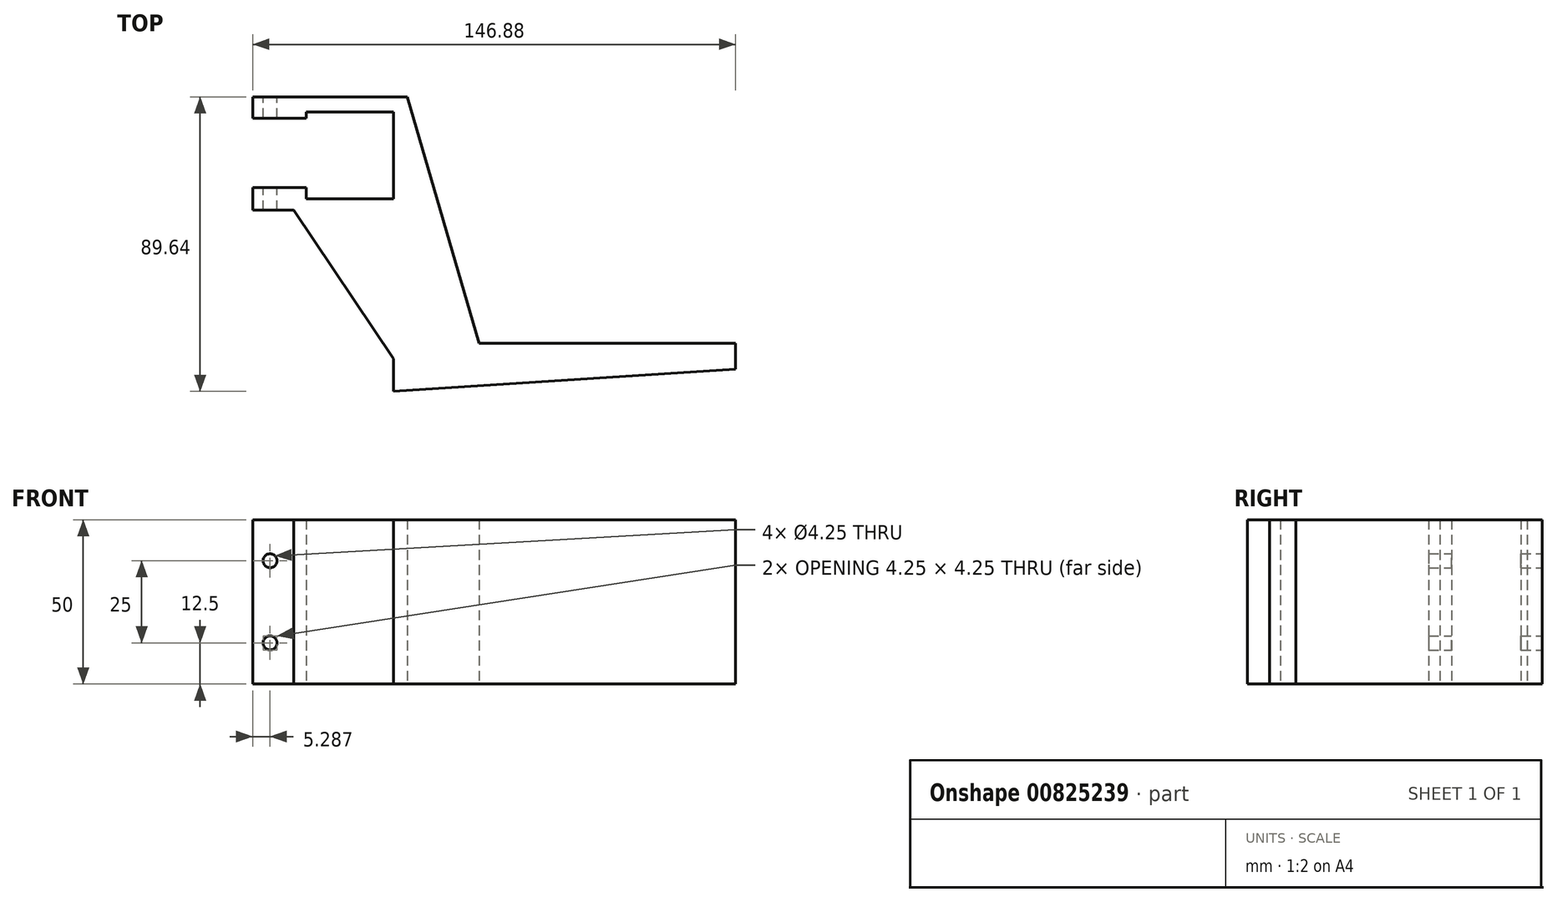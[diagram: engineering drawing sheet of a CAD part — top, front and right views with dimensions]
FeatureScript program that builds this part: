
annotation { "Feature Type Name" : "Feature", "Feature Type Description" : "" }
export const myFeature = defineFeature(function(context is Context, id is Id, definition is map)
    precondition{}
    {
        {
            var Q0;
            Q0=qCreatedBy(makeId("Top.planeOp"),FACE);
            var sketch = newSketch(context, id + "F0", { "sketchPlane" : qUnion([Q0])});
            skLineSegment(sketch, "E0", {"start": v(-30.27, 0) * mm, "end": v(-30.27, -1.89) * mm});
            skLineSegment(sketch, "E1", {"start": v(-30.27, -1.89) * mm, "end": v(-26.5, -1.89) * mm});
            skLineSegment(sketch, "E2", {"start": v(-26.5, -1.89) * mm, "end": v(-26.5, 0) * mm});
            skLineSegment(sketch, "E3", {"start": v(-26.5, 0) * mm, "end": v(0, 0) * mm});
            skLineSegment(sketch, "E4", {"start": v(0, 0) * mm, "end": v(0, -26.5) * mm});
            skLineSegment(sketch, "E5", {"start": v(0, -26.5) * mm, "end": v(-26.5, -26.5) * mm});
            skLineSegment(sketch, "E6", {"start": v(-30.27, -26.5) * mm, "end": v(-30.27, -29.91) * mm});
            skLineSegment(sketch, "E7", {"start": v(-30.27, -29.91) * mm, "end": v(0, -29.91) * mm});
            skLineSegment(sketch, "E8", {"start": v(0, -29.91) * mm, "end": v(4.22, -29.91) * mm});
            skLineSegment(sketch, "E9", {"start": v(4.22, -29.91) * mm, "end": v(4.22, 0) * mm});
            skLineSegment(sketch, "E10", {"start": v(4.22, 0) * mm, "end": v(4.22, 4.58) * mm});
            skLineSegment(sketch, "E11", {"start": v(4.22, 4.58) * mm, "end": v(-30.27, 4.58) * mm});
            skLineSegment(sketch, "E12", {"start": v(-30.27, 4.58) * mm, "end": v(-30.27, 0) * mm});
            skLineSegment(sketch, "E13", {"start": v(-26.5, -26.5) * mm, "end": v(-26.5, -22.97) * mm});
            skLineSegment(sketch, "E14", {"start": v(-26.5, -22.97) * mm, "end": v(-30.27, -22.97) * mm});
            skLineSegment(sketch, "E15", {"start": v(-30.27, -22.97) * mm, "end": v(-30.27, -26.5) * mm});
            skLineSegment(sketch, "E16", {"start": v(-30.27, 4.58) * mm, "end": v(-42.8, 4.58) * mm});
            skLineSegment(sketch, "E17", {"start": v(-42.8, 4.58) * mm, "end": v(-42.8, -1.89) * mm});
            skLineSegment(sketch, "E18", {"start": v(-42.8, -1.89) * mm, "end": v(-30.27, -1.89) * mm});
            skLineSegment(sketch, "E19", {"start": v(-30.27, -22.97) * mm, "end": v(-42.8, -22.97) * mm});
            skLineSegment(sketch, "E20", {"start": v(-42.8, -22.97) * mm, "end": v(-42.8, -29.91) * mm});
            skLineSegment(sketch, "E21", {"start": v(-42.8, -29.91) * mm, "end": v(-30.27, -29.91) * mm});
            skLineSegment(sketch, "E22", {"start": v(4.22, 4.58) * mm, "end": v(4.22, -70.37) * mm});
            skLineSegment(sketch, "E23", {"start": v(0, -29.91) * mm, "end": v(0, -75.04) * mm});
            skLineSegment(sketch, "E24", {"start": v(4.22, -70.37) * mm, "end": v(26.08, -70.37) * mm});
            skLineSegment(sketch, "E25", {"start": v(26.08, -70.37) * mm, "end": v(4.22, 4.58) * mm});
            skLineSegment(sketch, "E26", {"start": v(0, -75.04) * mm, "end": v(-30.27, -29.91) * mm});
            skLineSegment(sketch, "E27", {"start": v(0, -75.04) * mm, "end": v(0, -85.06) * mm});
            skLineSegment(sketch, "E28", {"start": v(104.1, -70.37) * mm, "end": v(104.1, -75.04) * mm});
            skLineSegment(sketch, "E29", {"start": v(104.1, -75.04) * mm, "end": v(104.1, -78.33) * mm});
            skLineSegment(sketch, "E30", {"start": v(26.08, -70.37) * mm, "end": v(104.1, -70.37) * mm});
            skLineSegment(sketch, "E31", {"start": v(0, -85.06) * mm, "end": v(104.1, -78.33) * mm});
            skSolve(sketch);
        }
        {
            var Q0;
            Q0=makeQuery(id+"F0.imprint","IMPRINT",FACE,{"disambiguationData":[TD([[makeQuery(id+"F0.imprint","IMPRINT",EDGE,{"derivedFrom":sQuery(id+"F0.wireOp",EDGE,"E0")}),1.0]])]});
            var Q1;
            Q1=makeQuery(id+"F0.imprint","IMPRINT",FACE,{"disambiguationData":[TD([[makeQuery(id+"F0.imprint","IMPRINT",EDGE,{"derivedFrom":sQuery(id+"F0.wireOp",EDGE,"E0")}),-1.0]])]});
            var Q2;
            Q2=makeQuery(id+"F0.imprint","IMPRINT",FACE,{"disambiguationData":[TD([[makeQuery(id+"F0.imprint","IMPRINT",EDGE,{"derivedFrom":sQuery(id+"F0.wireOp",EDGE,"E6")}),-1.0]])]});
            var Q3;
            Q3=makeQuery(id+"F0.imprint","IMPRINT",FACE,{"disambiguationData":[TD([[makeQuery(id+"F0.imprint","IMPRINT",EDGE,{"derivedFrom":sQuery(id+"F0.wireOp",EDGE,"E7")}),-1.0]])]});
            var Q4;
            Q4=makeQuery(id+"F0.imprint","IMPRINT",FACE,{"disambiguationData":[TD([[makeQuery(id+"F0.imprint","IMPRINT",EDGE,{"derivedFrom":sQuery(id+"F0.wireOp",EDGE,"i6da61lU-EC8u-8acG-F84r-jOoYWlgI5SIy")}),-1.0]])]});
            var Q5;
            {var subQ1=sQuery(id+"F0.wireOp",EDGE,"E8");Q5=makeQuery(id+"F0.imprint","IMPRINT",FACE,{"disambiguationData":[TD([[makeQuery(id+"F0.imprint","IMPRINT",EDGE,{"derivedFrom":subQ1}),-1.0]])]});}
            var Q6;
            {var subQ3=sQuery(id+"F0.wireOp",EDGE,"E24");Q6=makeQuery(id+"F0.imprint","IMPRINT",FACE,{"disambiguationData":[TD([[makeQuery(id+"F0.imprint","IMPRINT",EDGE,{"derivedFrom":subQ3}),1.0]])]});}
            extrude(context, id + "F1", {"entities" : qUnion([Q0, Q1, Q2, Q3, Q4, Q5, Q6]), "depth" : 50 * mm, "offsetDistance" : 25 * mm});
        }
        {
            var Q0;
            Q0=makeQuery(id+"F1.opExtrude","SWEPT_FACE",FACE,{"disambiguationData":[OSD([sQuery(id+"F0.wireOp",EDGE,"E11"),sQuery(id+"F0.wireOp",EDGE,"E16")])]});
            var sketch = newSketch(context, id + "F2", { "sketchPlane" : qUnion([Q0])});
            skLineSegment(sketch, "E32", {"start": v(42.8, 50) * mm, "end": v(42.8, 25) * mm});
            skLineSegment(sketch, "E33", {"start": v(42.8, 25) * mm, "end": v(42.8, 0) * mm});
            skLineSegment(sketch, "E34", {"start": v(42.8, 0) * mm, "end": v(42.8, 12.5) * mm});
            skLineSegment(sketch, "E35", {"start": v(42.8, 12.5) * mm, "end": v(42.8, 37.5) * mm});
            skLineSegment(sketch, "E36", {"start": v(42.8, 50) * mm, "end": v(37.5, 50) * mm});
            skPoint(sketch, "E37", {"position": v(37.5, 37.5) * mm});
            skPoint(sketch, "E38", {"position": v(37.5, 12.5) * mm});
            skSolve(sketch);
        }
        {
            var Q0;
            Q0=sQuery(id+"F2.wireOp",VERTEX,"E37");
            var Q1;
            Q1=sQuery(id+"F2.wireOp",VERTEX,"E38");
            var Q2;
            Q2=makeQuery(id+"F1.opExtrude","SWEPT_BODY",BODY,{"disambiguationData":[OSD([sQuery(id+"F0.wireOp",EDGE,"E1"),sQuery(id+"F0.wireOp",EDGE,"E2"),sQuery(id+"F0.wireOp",EDGE,"E3"),sQuery(id+"F0.wireOp",EDGE,"E4"),sQuery(id+"F0.wireOp",EDGE,"E5"),sQuery(id+"F0.wireOp",EDGE,"E11"),sQuery(id+"F0.wireOp",EDGE,"E13"),sQuery(id+"F0.wireOp",EDGE,"E14"),sQuery(id+"F0.wireOp",EDGE,"E16"),sQuery(id+"F0.wireOp",EDGE,"E17"),sQuery(id+"F0.wireOp",EDGE,"E18"),sQuery(id+"F0.wireOp",EDGE,"E19"),sQuery(id+"F0.wireOp",EDGE,"E20"),sQuery(id+"F0.wireOp",EDGE,"E21"),sQuery(id+"F0.wireOp",EDGE,"0hNsv3Ce-IlmC-cHQo-ni2x-AnQ9uOAgxHR4"),sQuery(id+"F0.wireOp",EDGE,"c165P6iI-nRFD-T6o3-SvL0-4ZNoRffguBie"),sQuery(id+"F0.wireOp",EDGE,"E25"),sQuery(id+"F0.wireOp",EDGE,"E26"),sQuery(id+"F0.wireOp",EDGE,"E27"),sQuery(id+"F0.wireOp",EDGE,"DnOOU8Wi-WvfL-K6H4-AOTD-4AKdZAOfW9X8")])]});
            hole(context, id + "F3", {"style" : HoleStyle.SIMPLE, "endStyle" : HoleEndStyle.THROUGH, "holeDiameter" : 4.25 * mm, "majorDiameter" : 5 * mm, "isTappedThrough" : true, "tappedDepth" : 12 * mm, "tapClearance" : 3, "locations" : qUnion([Q0, Q1]), "scope" : qUnion([Q2])});
        }
    });
